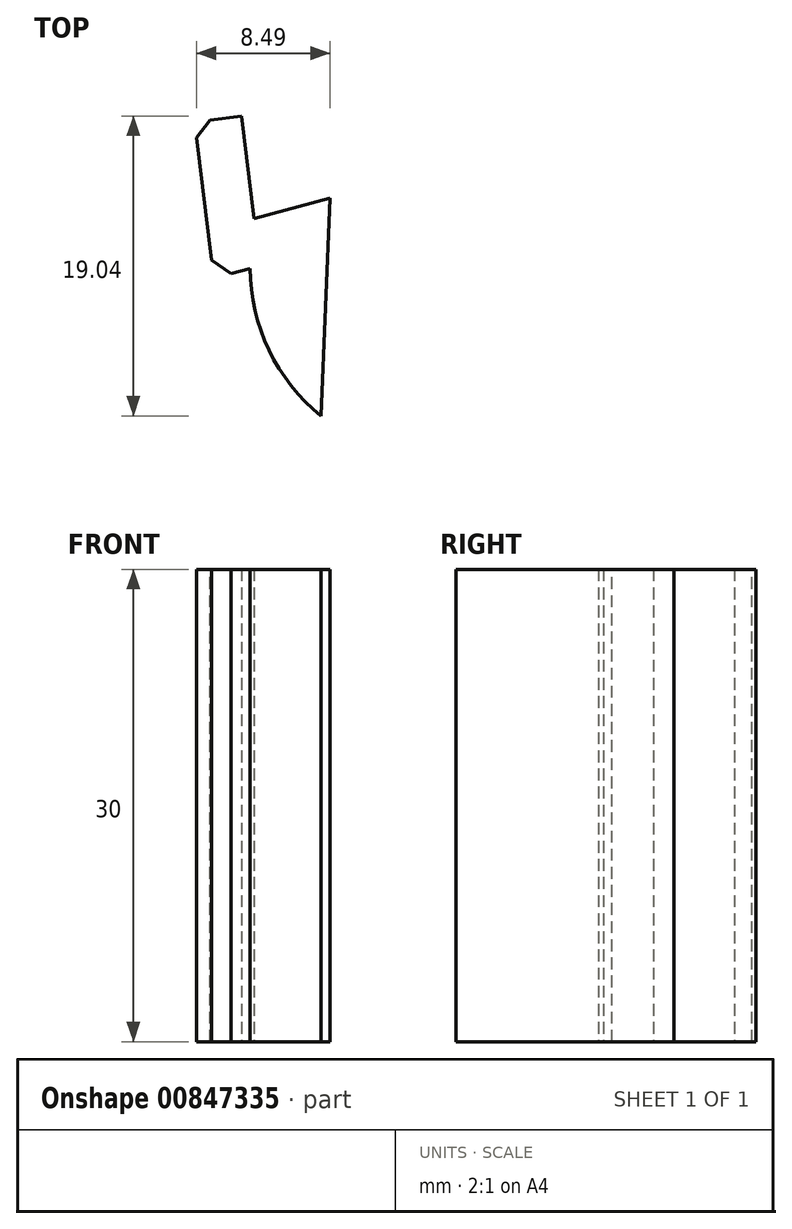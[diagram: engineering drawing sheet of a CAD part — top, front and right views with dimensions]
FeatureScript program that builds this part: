
annotation { "Feature Type Name" : "Feature", "Feature Type Description" : "" }
export const myFeature = defineFeature(function(context is Context, id is Id, definition is map)
    precondition{}
    {
        {
            var Q0;
            Q0=qCreatedBy(makeId("Top.planeOp"),FACE);
            var sketch = newSketch(context, id + "F0", { "sketchPlane" : qUnion([Q0])});
            skCircle(sketch, "E0", {"center": v(0, 0) * mm, "radius": 12 * mm});
            skCircle(sketch, "E1", {"center": v(0, 0) * mm, "radius": 10 * mm});
            skPoint(sketch, "E2", {"position": v(-10, 0) * mm});
            skLineSegment(sketch, "E3", {"start": v(-14.32, -0.62) * mm, "end": v(-15.54, 9.3) * mm});
            skPoint(sketch, "E4", {"position": v(-12, 0) * mm});
            skLineSegment(sketch, "E5", {"start": v(-15.54, 9.3) * mm, "end": v(-12.56, 9.67) * mm});
            skLineSegment(sketch, "E6", {"start": v(-12.56, 9.67) * mm, "end": v(-11.76, 3.17) * mm});
            skLineSegment(sketch, "E7", {"start": v(-11.76, 3.17) * mm, "end": v(-6.93, 4.46) * mm});
            skLineSegment(sketch, "E8", {"start": v(-6.93, 4.46) * mm, "end": v(-7.5, -9.37) * mm});
            skLineSegment(sketch, "E9", {"start": v(-14.32, -0.62) * mm, "end": v(-12, 0) * mm});
            skSolve(sketch);
        }
        {
            var Q0;
            {var subQ0=sQuery(id+"F0.wireOp",EDGE,"UKEWEX0W-URwR-FJGD-bFrx-5N3lhZb1MriB");Q0=makeQuery(id+"F0.imprint","IMPRINT",FACE,{"disambiguationData":[TD([[makeQuery(id+"F0.imprint","IMPRINT",EDGE,{"derivedFrom":subQ0}),-1.0]])]});}
            var Q1;
            {var subQ5=sQuery(id+"F0.wireOp",EDGE,"E0");var subQ6=makeQuery(id+"F0.imprint","INTERSECT",VERTEX,{"derivedFrom":[subQ5,sQuery(id+"F0.wireOp",EDGE,"UKEWEX0W-URwR-FJGD-bFrx-5N3lhZb1MriB")]});Q1=makeQuery(id+"F0.imprint","IMPRINT",FACE,{"disambiguationData":[TD([[makeQuery(id+"F0.imprint","IMPRINT",EDGE,{"disambiguationData":[TD([[subQ6,1.0]])],"derivedFrom":subQ5}),1.0]])]});}
            var Q2;
            {var subQ0=sQuery(id+"F0.wireOp",EDGE,"E7");var subQ1=sQuery(id+"F0.wireOp",EDGE,"E1");var subQ2=makeQuery(id+"F0.imprint","INTERSECT",VERTEX,{"derivedFrom":[subQ1,subQ0]});Q2=makeQuery(id+"F0.imprint","IMPRINT",FACE,{"disambiguationData":[TD([[makeQuery(id+"F0.imprint","IMPRINT",EDGE,{"disambiguationData":[TD([[subQ2,-1.0]])],"derivedFrom":subQ1}),1.0]])]});}
            var Q3;
            Q3=makeQuery(id+"F0.imprint","IMPRINT",FACE,{"disambiguationData":[TD([[makeQuery(id+"F0.imprint","IMPRINT",EDGE,{"derivedFrom":sQuery(id+"F0.wireOp",EDGE,"E3")}),-1.0]])]});
            extrude(context, id + "F1", {"entities" : qUnion([Q0, Q1, Q2, Q3]), "depth" : 30 * mm, "offsetDistance" : 25 * mm});
        }
        {
            var Q0;
            Q0=makeQuery(id+"F1.opExtrude","CAP_FACE",FACE,{"disambiguationData":[OSD([sQuery(id+"F0.wireOp",EDGE,"E0")])],"isStart":false});
            var sketch = newSketch(context, id + "F2", { "sketchPlane" : qUnion([Q0])});
            skLineSegment(sketch, "E10.bottom", {"start": v(20.84, -6.76) * mm, "end": v(-19.16, -6.76) * mm});
            skLineSegment(sketch, "E10.top", {"start": v(20.84, 13.24) * mm, "end": v(-19.16, 13.24) * mm});
            skLineSegment(sketch, "E10.left", {"start": v(20.84, -6.76) * mm, "end": v(20.84, 13.24) * mm});
            skLineSegment(sketch, "E10.right", {"start": v(-19.16, -6.76) * mm, "end": v(-19.16, 13.24) * mm});
            skSolve(sketch);
        }
        {
            var Q0;
            Q0=makeQuery(id+"F1.opExtrude","SWEPT_EDGE",EDGE,{"disambiguationData":[OSD([sQuery(id+"F0.wireOp",EDGE,"UKEWEX0W-URwR-FJGD-bFrx-5N3lhZb1MriB"),sQuery(id+"F0.wireOp",EDGE,"E3")])]});
            chamfer(context, id + "F3", {"entities" : qUnion([Q0]), "width" : 1 * mm, "tangentPropagation" : true});
        }
    });
